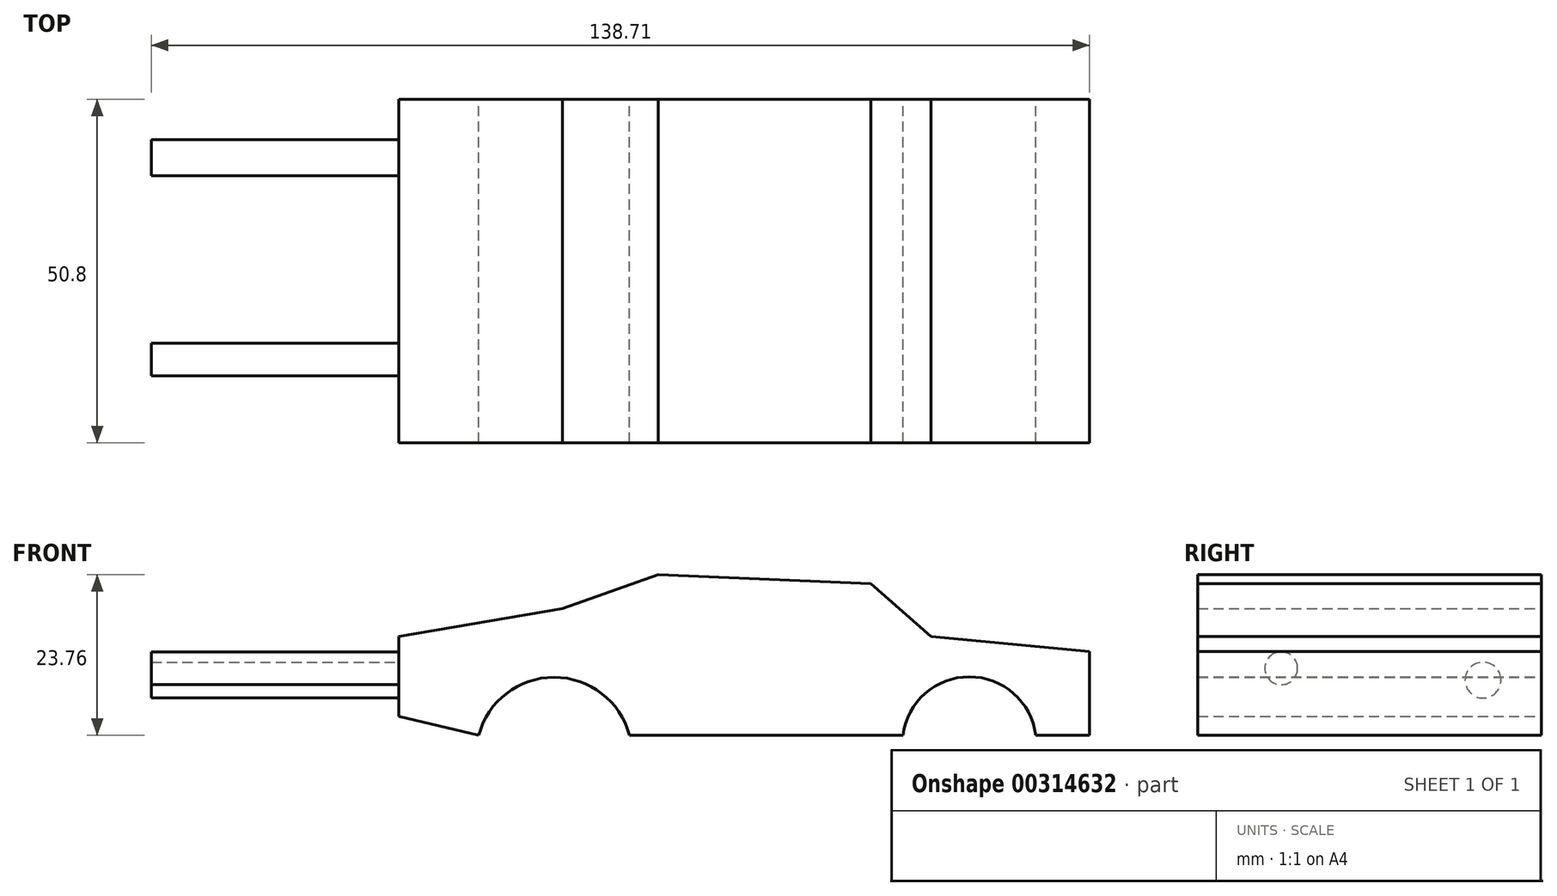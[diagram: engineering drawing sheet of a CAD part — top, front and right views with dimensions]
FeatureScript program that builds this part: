
annotation { "Feature Type Name" : "Feature", "Feature Type Description" : "" }
export const myFeature = defineFeature(function(context is Context, id is Id, definition is map)
    precondition{}
    {
        {
            var Q0;
            Q0=qCreatedBy(makeId("Front.planeOp"),FACE);
            var sketch = newSketch(context, id + "F0", { "sketchPlane" : qUnion([Q0])});
            skLineSegment(sketch, "E0", {"start": v(-93.96, 5.53) * mm, "end": v(-53.52, 5.53) * mm});
            skArc(sketch, "E1", {"start": v(-93.96, 5.53) * mm, "mid": v(-105.1, 14.11) * mm, "end": v(-116.25, 5.53) * mm});
            skArc(sketch, "E2", {"start": v(-33.89, 5.53) * mm, "mid": v(-43.7, 14.19) * mm, "end": v(-53.52, 5.53) * mm});
            skLineSegment(sketch, "E3", {"start": v(-116.25, 5.53) * mm, "end": v(-128.05, 8.33) * mm});
            skLineSegment(sketch, "E4", {"start": v(-128.05, 8.33) * mm, "end": v(-128.05, 20.14) * mm});
            skLineSegment(sketch, "E5", {"start": v(-128.05, 20.14) * mm, "end": v(-103.85, 24.27) * mm});
            skLineSegment(sketch, "E6", {"start": v(-103.85, 24.27) * mm, "end": v(-89.68, 29.3) * mm});
            skLineSegment(sketch, "E7", {"start": v(-89.68, 29.3) * mm, "end": v(-58.24, 27.96) * mm});
            skLineSegment(sketch, "E8", {"start": v(-58.24, 27.96) * mm, "end": v(-49.39, 20.14) * mm});
            skLineSegment(sketch, "E9", {"start": v(-49.39, 20.14) * mm, "end": v(-25.92, 17.93) * mm});
            skLineSegment(sketch, "E10", {"start": v(-25.92, 17.93) * mm, "end": v(-25.92, 5.53) * mm});
            skLineSegment(sketch, "E11", {"start": v(-25.92, 5.53) * mm, "end": v(-33.89, 5.53) * mm});
            skSolve(sketch);
        }
        {
            var Q0;
            Q0=makeQuery(id+"F0.imprint","IMPRINT",FACE,{"disambiguationData":[TD([[makeQuery(id+"F0.imprint","IMPRINT",EDGE,{"derivedFrom":sQuery(id+"F0.wireOp",EDGE,"E0")}),1.0]])]});
            extrude(context, id + "F1", {"entities" : qUnion([Q0]), "depth" : 25.4 * mm});
        }
        {
            var Q0;
            Q0=makeQuery(id+"F1.opExtrude","CAP_FACE",FACE,{"disambiguationData":[OSD([sQuery(id+"F0.wireOp",EDGE,"E0"),sQuery(id+"F0.wireOp",EDGE,"E1"),sQuery(id+"F0.wireOp",EDGE,"E2"),sQuery(id+"F0.wireOp",EDGE,"E3"),sQuery(id+"F0.wireOp",EDGE,"E4"),sQuery(id+"F0.wireOp",EDGE,"E5"),sQuery(id+"F0.wireOp",EDGE,"E6"),sQuery(id+"F0.wireOp",EDGE,"E7"),sQuery(id+"F0.wireOp",EDGE,"E8"),sQuery(id+"F0.wireOp",EDGE,"E9"),sQuery(id+"F0.wireOp",EDGE,"E10"),sQuery(id+"F0.wireOp",EDGE,"E11")])],"isStart":true});
            extrude(context, id + "F2", {"entities" : qUnion([Q0]), "operationType" : NewBodyOperationType.ADD, "depth" : 25.4 * mm});
        }
        {
            var Q0;
            {var subQ0=sQuery(id+"F0.wireOp",EDGE,"E4");Q0=makeQuery(id+"F2.boolean.opBoolean","MERGE",FACE,{"derivedFrom":[makeQuery(id+"F1.opExtrude","SWEPT_FACE",FACE,{"disambiguationData":[OSD([subQ0])]}),makeQuery(id+"F2.opExtrude","SWEPT_FACE",FACE,{"disambiguationData":[OSD([subQ0])]})]});}
            var sketch = newSketch(context, id + "F3", { "sketchPlane" : qUnion([Q0])});
            skCircle(sketch, "E12", {"center": v(-16.75, 13.69) * mm, "radius": 2.65 * mm});
            skCircle(sketch, "E13", {"center": v(13.1, 15.44) * mm, "radius": 2.43 * mm});
            skSolve(sketch);
        }
        {
            var Q0;
            Q0 = qSketchRegion(id + "F3", true);
            extrude(context, id + "F4", {"entities" : qUnion([Q0]), "operationType" : NewBodyOperationType.ADD, "depth" : 36.58 * mm});
        }
    });
